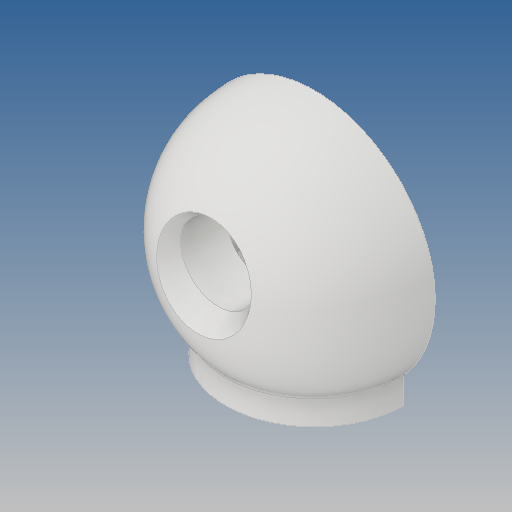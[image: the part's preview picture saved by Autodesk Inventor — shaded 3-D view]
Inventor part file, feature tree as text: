
AUTODESK INVENTOR PART (.ipt)
format: ipt  version: 2020 (Build 240168000, 168)  size: 448,000 bytes
history: native  units: mm
features: reference x24, sketch x23, extrude x17, other x11, revolve x7, projected_geometry x4, fillet x1
ambient origin geometry x8: Origin, YZ Plane, XZ Plane, XY Plane, X Axis, Y Axis, Z Axis, Center Point
bodies: Body1 (feature_tree)
feature tree (87):
  other  "Твердое тело1"
  other  "РабПлоскость1"
  revolve  "Вращение1"
  sketch  "Эскиз2"
  other  "РабПлоскость2"
  revolve  "Вращение2"
  extrude  "Выдавливание1"  TaperAngle=180.0deg  [1 undecoded]
  extrude  "Выдавливание2"  Depth=1.0mm
  revolve  "Вращение3"
  revolve  "Вращение4"
  sketch  "Эскиз8"
  revolve  "Вращение5"
  revolve  "Вращение6"
  revolve  "Вращение7"
  other  "РабПлоскость3"
  extrude  "Выдавливание3"  Depth=1.0mm
  sketch  "Эскиз11"
  extrude  "Выдавливание4"  Depth=1.0mm
  extrude  "Выдавливание5"  Depth=2.0mm
  extrude  "Выдавливание6"  TaperAngle=180.0deg  [1 undecoded]
  extrude  "Выдавливание7"  Depth=0.5mm
  fillet  "Сопряжение1"  Radius=0.5mm
  extrude  "Выдавливание8"  Depth=0.5mm
  extrude  "Выдавливание9"  Depth=0.5mm
  extrude  "Выдавливание10"  Depth=0.5mm
  extrude  "Выдавливание11"  Depth=0.5mm
  extrude  "Выдавливание12"  Depth=0.5mm
  extrude  "Выдавливание13"  Depth=0.5mm
  extrude  "Выдавливание14"  Depth=0.5mm
  extrude  "Выдавливание15"  Depth=0.5mm
  extrude  "Выдавливание16"  Depth=0.5mm
  extrude  "Выдавливание17"  Depth=10.0mm TaperAngle=0.0deg
  sketch  "Эскиз1"
  reference  "Ссылка1"
  reference  "Ссылка2"
  reference  "Ссылка3"
  sketch  "Эскиз3"
  reference  "Ссылка4"
  projected_geometry  "Спроецированная петля1"
  reference  "Ссылка5"
  sketch  "Эскиз4"
  reference  "Ссылка6"
  reference  "Ссылка7"
  reference  "Ссылка8"
  reference  "Ссылка9"
  reference  "Ссылка10"
  reference  "Ссылка11"
  reference  "Ссылка12"
  reference  "Ссылка13"
  reference  "Ссылка14"
  reference  "Ссылка15"
  reference  "Ссылка16"
  reference  "Ссылка17"
  reference  "Ссылка18"
  reference  "Ссылка19"
  reference  "Ссылка20"
  sketch  "Эскиз5"
  sketch  "Эскиз6"
  sketch  "Эскиз7"
  sketch  "Эскиз9"
  sketch  "Эскиз10"
  sketch  "Эскиз12"
  sketch  "Эскиз13"
  projected_geometry  "Спроецированная петля2"
  sketch  "Эскиз14"
  sketch  "Эскиз15"
  reference  "Ссылка21"
  reference  "Ссылка22"
  reference  "Ссылка23"
  reference  "Ссылка24"
  sketch  "Эскиз16"
  sketch  "Эскиз17"
  other  "Твердое тело2"
  sketch  "Эскиз18"
  projected_geometry  "Спроецированная петля3"
  sketch  "Эскиз19"
  projected_geometry  "Спроецированная петля4"
  sketch  "Эскиз20"
  sketch  "Эскиз21"
  sketch  "Эскиз22"
  sketch  "Эскиз23"
  other  "<userpath>\Desktop\Робот_Инст\ROBOT_FULL\Camera OV7670.iam"
  other  "Camera OV7670.iam"
  other  "CAMERA_COVER_1:1"
  other  "CameraLens_2"
  other  "PcbForCamera_1"
  parser-record x1  (decoder bookkeeping rows leaked as tree rows — omitted from the tree; the rows remain in map.json)
note: 2 required parameter values undecoded (feature->parameter linkage not recoverable at this tier; creation-order binding heuristic only, values carry confidence <= 0.55)
note: 1 file-system path scrubbed to <path> (originals preserved in map.json)
